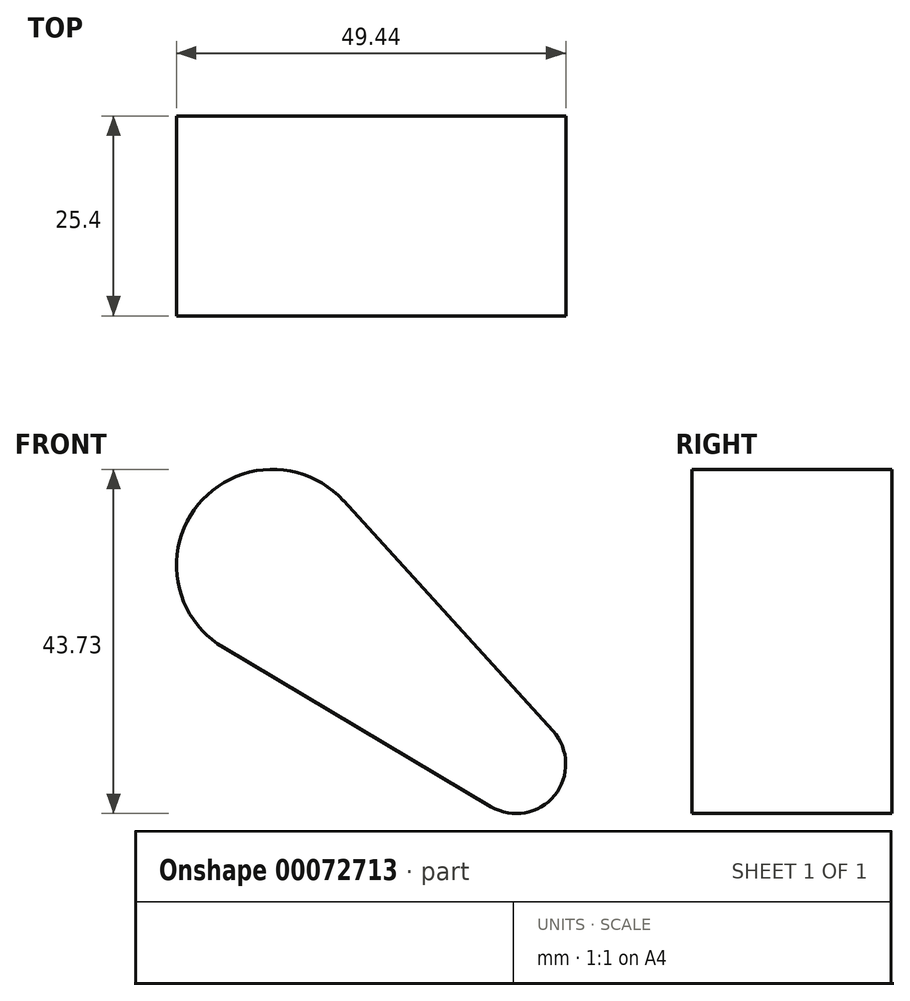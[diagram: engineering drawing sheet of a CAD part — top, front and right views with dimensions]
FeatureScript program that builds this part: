
annotation { "Feature Type Name" : "Feature", "Feature Type Description" : "" }
export const myFeature = defineFeature(function(context is Context, id is Id, definition is map)
    precondition{}
    {
        {
            var Q0;
            Q0=qCreatedBy(makeId("Front.planeOp"),FACE);
            var sketch = newSketch(context, id + "F0", { "sketchPlane" : qUnion([Q0])});
            skArc(sketch, "E0", {"start": v(-18.8, 31.96) * mm, "mid": v(-37.23, 31.46) * mm, "end": v(-34.01, 13.3) * mm});
            skArc(sketch, "E1", {"start": v(0, -6.91) * mm, "mid": v(8.06, -5.48) * mm, "end": v(7.84, 2.7) * mm});
            skLineSegment(sketch, "E2", {"start": v(-34.01, 13.3) * mm, "end": v(0, -6.91) * mm});
            skLineSegment(sketch, "E3", {"start": v(-18.8, 31.96) * mm, "end": v(7.84, 2.7) * mm});
            skSolve(sketch);
        }
        {
            var Q0;
            {var subQ0=sQuery(id+"F0.wireOp",EDGE,"E0");var subQ1=makeQuery(id+"F0.imprint","INTERSECT",VERTEX,{"derivedFrom":[subQ0,sQuery(id+"F0.wireOp",EDGE,"E2")]});Q0=makeQuery(id+"F0.imprint","IMPRINT",FACE,{"disambiguationData":[TD([[makeQuery(id+"F0.imprint","IMPRINT",EDGE,{"disambiguationData":[TD([[subQ1,1.0]])],"derivedFrom":subQ0}),1.0]])]});}
            var Q1;
            {var subQ0=sQuery(id+"F0.wireOp",EDGE,"E2");Q1=makeQuery(id+"F0.imprint","IMPRINT",FACE,{"disambiguationData":[TD([[makeQuery(id+"F0.imprint","IMPRINT",EDGE,{"derivedFrom":subQ0}),1.0]])]});}
            var Q2;
            {var subQ0=sQuery(id+"F0.wireOp",EDGE,"E1");var subQ1=makeQuery(id+"F0.imprint","INTERSECT",VERTEX,{"derivedFrom":[subQ0,sQuery(id+"F0.wireOp",EDGE,"E2")]});Q2=makeQuery(id+"F0.imprint","IMPRINT",FACE,{"disambiguationData":[TD([[makeQuery(id+"F0.imprint","IMPRINT",EDGE,{"disambiguationData":[TD([[subQ1,1.0]])],"derivedFrom":subQ0}),1.0]])]});}
            extrude(context, id + "F1", {"entities" : qUnion([Q0, Q1, Q2]), "depth" : 25.4 * mm});
        }
    });
